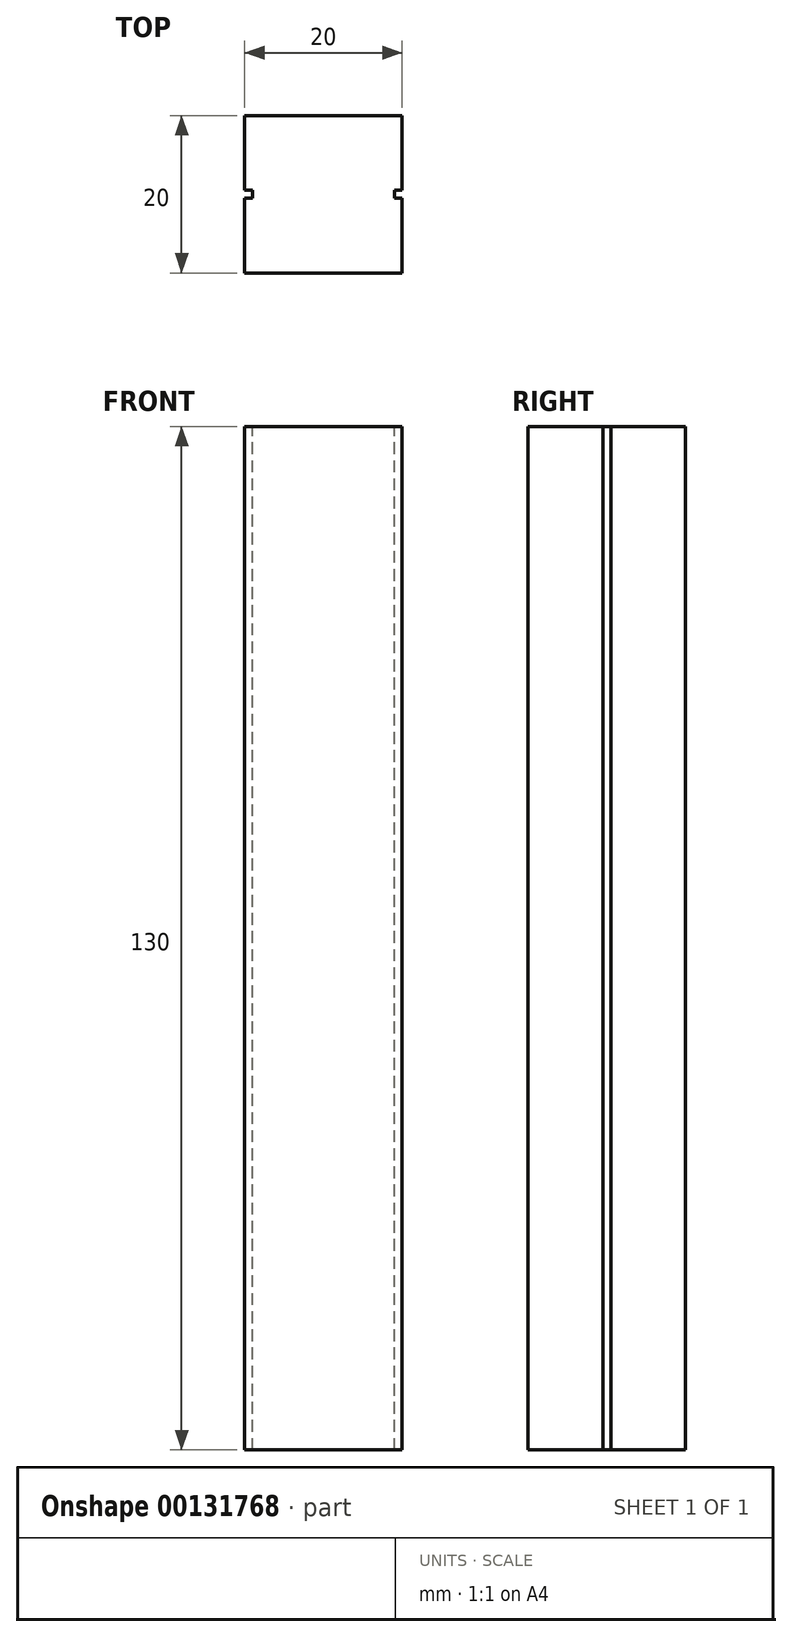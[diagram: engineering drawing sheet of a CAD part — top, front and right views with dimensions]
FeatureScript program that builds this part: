
annotation { "Feature Type Name" : "Feature", "Feature Type Description" : "" }
export const myFeature = defineFeature(function(context is Context, id is Id, definition is map)
    precondition{}
    {
        {
            var Q0;
            Q0=qCreatedBy(makeId("Top.planeOp"),FACE);
            var sketch = newSketch(context, id + "F0", { "sketchPlane" : qUnion([Q0])});
            skLineSegment(sketch, "E0.bottom", {"start": v(10, 10) * mm, "end": v(-10, 10) * mm});
            skLineSegment(sketch, "E0.top", {"start": v(10, -10) * mm, "end": v(-10, -10) * mm});
            skLineSegment(sketch, "E0.left", {"start": v(10, 10) * mm, "end": v(10, -10) * mm});
            skLineSegment(sketch, "E0.right", {"start": v(-10, 10) * mm, "end": v(-10, -10) * mm});
            skPoint(sketch, "E0.middle", {"position": v(0, 0) * mm});
            skSolve(sketch);
        }
        {
            var Q0;
            Q0=makeQuery(id+"F0.imprint","IMPRINT",FACE,{"disambiguationData":[TD([[makeQuery(id+"F0.imprint","IMPRINT",EDGE,{"derivedFrom":sQuery(id+"F0.wireOp",EDGE,"E0.bottom")}),1.0]])]});
            extrude(context, id + "F1", {"entities" : qUnion([Q0]), "depth" : 130 * mm});
        }
        {
            var Q0;
            Q0=makeQuery(id+"F1.opExtrude","CAP_FACE",FACE,{"disambiguationData":[OSD([sQuery(id+"F0.wireOp",EDGE,"E0.bottom"),sQuery(id+"F0.wireOp",EDGE,"E0.top"),sQuery(id+"F0.wireOp",EDGE,"E0.left"),sQuery(id+"F0.wireOp",EDGE,"E0.right")])],"isStart":false});
            var sketch = newSketch(context, id + "F2", { "sketchPlane" : qUnion([Q0])});
            skSolve(sketch);
        }
        {
            var Q0;
            Q0=makeQuery(id+"F2.imprint","IMPRINT",FACE,{"disambiguationData":[TD([[makeQuery(id+"F2.imprint","IMPRINT",EDGE,{"derivedFrom":makeQuery(id+"F1.opExtrude","CAP_EDGE",EDGE,{"disambiguationData":[OSD([sQuery(id+"F0.wireOp",EDGE,"E0.bottom")])],"isStart":false})}),1.0]])]});
            var sketch = newSketch(context, id + "F3", { "sketchPlane" : qUnion([Q0])});
            skLineSegment(sketch, "E1.0", {"start": v(10, 10) * mm, "end": v(-10, 10) * mm});
            skLineSegment(sketch, "E2.0", {"start": v(-10, 10) * mm, "end": v(-10, -10) * mm});
            skLineSegment(sketch, "E3.0", {"start": v(10, -10) * mm, "end": v(-10, -10) * mm});
            skLineSegment(sketch, "E4.0", {"start": v(10, 10) * mm, "end": v(10, -10) * mm});
            skLineSegment(sketch, "E5.bottom", {"start": v(-0.5, 10) * mm, "end": v(0.5, 10) * mm});
            skLineSegment(sketch, "E5.top", {"start": v(-0.5, 9) * mm, "end": v(0.5, 9) * mm});
            skLineSegment(sketch, "E5.left", {"start": v(-0.5, 10) * mm, "end": v(-0.5, 9) * mm});
            skLineSegment(sketch, "E5.right", {"start": v(0.5, 10) * mm, "end": v(0.5, 9) * mm});
            skLineSegment(sketch, "E6.bottom", {"start": v(10, 0.5) * mm, "end": v(9, 0.5) * mm});
            skLineSegment(sketch, "E6.top", {"start": v(10, -0.5) * mm, "end": v(9, -0.5) * mm});
            skLineSegment(sketch, "E6.left", {"start": v(10, 0.5) * mm, "end": v(10, -0.5) * mm});
            skLineSegment(sketch, "E6.right", {"start": v(9, 0.5) * mm, "end": v(9, -0.5) * mm});
            skLineSegment(sketch, "E7.bottom", {"start": v(0.5, -10) * mm, "end": v(-0.5, -10) * mm});
            skLineSegment(sketch, "E7.top", {"start": v(0.5, -9) * mm, "end": v(-0.5, -9) * mm});
            skLineSegment(sketch, "E7.left", {"start": v(0.5, -10) * mm, "end": v(0.5, -9) * mm});
            skLineSegment(sketch, "E7.right", {"start": v(-0.5, -10) * mm, "end": v(-0.5, -9) * mm});
            skLineSegment(sketch, "E8.bottom", {"start": v(-10, -0.5) * mm, "end": v(-9, -0.5) * mm});
            skLineSegment(sketch, "E8.top", {"start": v(-10, 0.5) * mm, "end": v(-9, 0.5) * mm});
            skLineSegment(sketch, "E8.left", {"start": v(-10, -0.5) * mm, "end": v(-10, 0.5) * mm});
            skLineSegment(sketch, "E8.right", {"start": v(-9, -0.5) * mm, "end": v(-9, 0.5) * mm});
            skSolve(sketch);
        }
        {
            var Q0;
            Q0=makeQuery(id+"F3.imprint","IMPRINT",FACE,{"disambiguationData":[TD([[makeQuery(id+"F3.imprint","IMPRINT",EDGE,{"derivedFrom":sQuery(id+"F3.wireOp",EDGE,"E8.bottom")}),1.0]])]});
            var Q1;
            Q1=makeQuery(id+"F3.imprint","IMPRINT",FACE,{"disambiguationData":[TD([[makeQuery(id+"F3.imprint","IMPRINT",EDGE,{"derivedFrom":sQuery(id+"F3.wireOp",EDGE,"E5.bottom")}),1.0]])]});
            var Q2;
            Q2=makeQuery(id+"F3.imprint","IMPRINT",FACE,{"disambiguationData":[TD([[makeQuery(id+"F3.imprint","IMPRINT",EDGE,{"derivedFrom":sQuery(id+"F3.wireOp",EDGE,"E6.bottom")}),1.0]])]});
            var Q3;
            Q3=makeQuery(id+"F3.imprint","IMPRINT",FACE,{"disambiguationData":[TD([[makeQuery(id+"F3.imprint","IMPRINT",EDGE,{"derivedFrom":sQuery(id+"F3.wireOp",EDGE,"E7.bottom")}),-1.0]])]});
            extrude(context, id + "F4", {"entities" : qUnion([Q0, Q1, Q2, Q3]), "operationType" : NewBodyOperationType.REMOVE, "endBound" : BoundingType.THROUGH_ALL, "oppositeDirection" : true, "depth" : 25 * mm});
        }
    });
